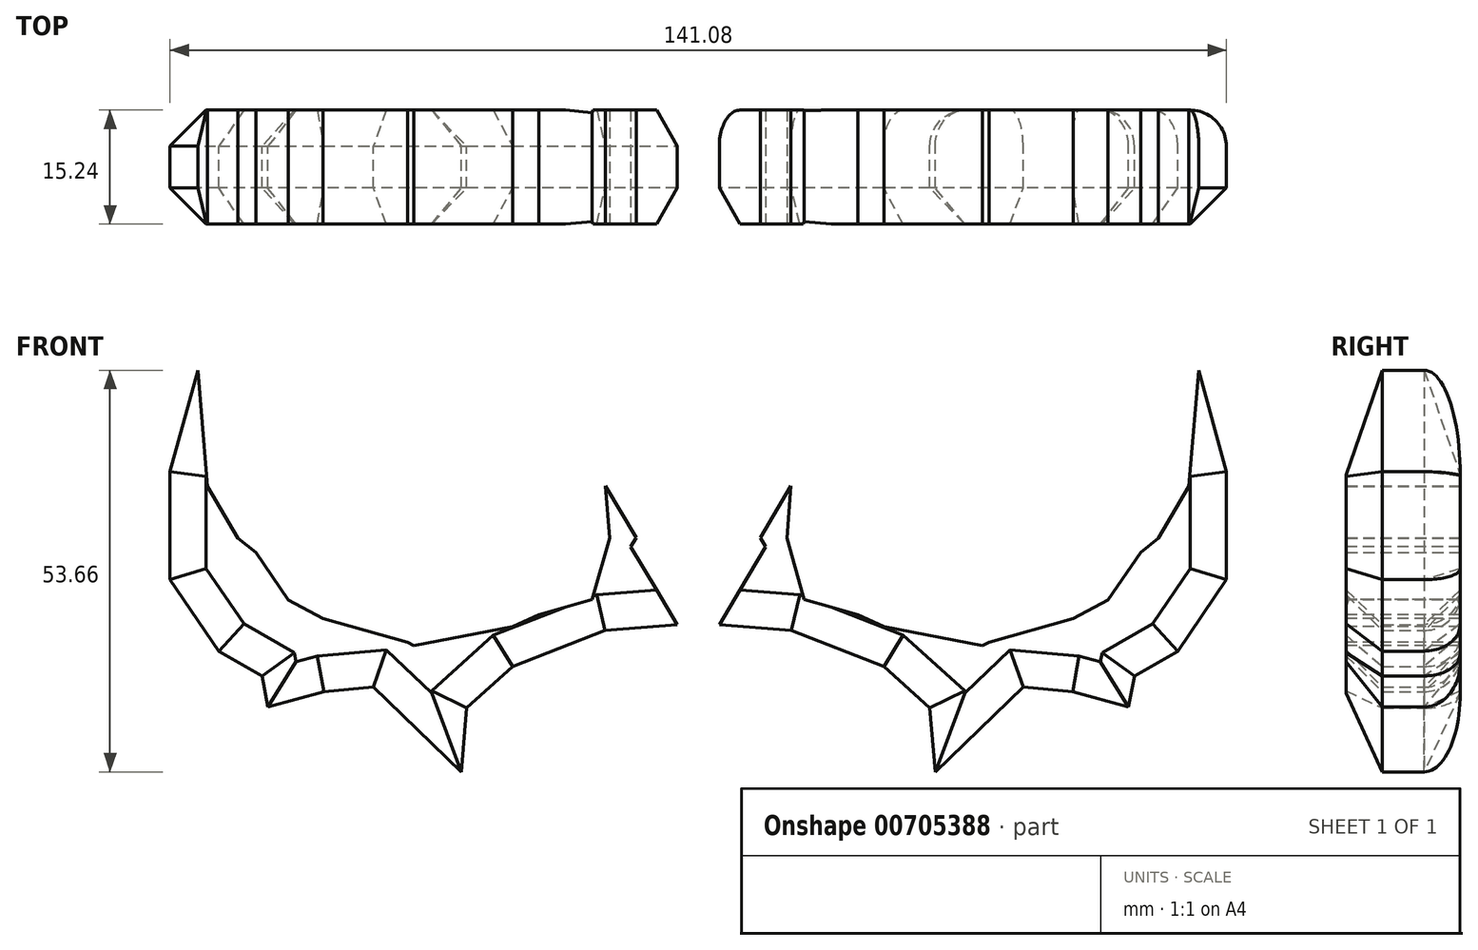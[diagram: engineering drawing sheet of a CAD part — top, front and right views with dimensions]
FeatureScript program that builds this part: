
annotation { "Feature Type Name" : "Feature", "Feature Type Description" : "" }
export const myFeature = defineFeature(function(context is Context, id is Id, definition is map)
    precondition{}
    {
        {
            var Q0;
            Q0=qCreatedBy(makeId("Front.planeOp"),FACE);
            var sketch = newSketch(context, id + "F0", { "sketchPlane" : qUnion([Q0])});
            skLineSegment(sketch, "E0", {"start": v(0, 0) * mm, "end": v(0, -3.04) * mm});
            skLineSegment(sketch, "E1", {"start": v(0, -3.04) * mm, "end": v(0, 0) * mm});
            skLineSegment(sketch, "E2", {"start": v(0, 15.49) * mm, "end": v(-8.28, 1.23) * mm});
            skLineSegment(sketch, "E3", {"start": v(-8.28, 1.23) * mm, "end": v(-12.37, 8.16) * mm});
            skLineSegment(sketch, "E4", {"start": v(-12.37, 8.16) * mm, "end": v(-11.9, 16.15) * mm});
            skFitSpline(sketch, "E5", {"points": [v(-11.9, 16.15) * mm, v(-15.37, 17.85) * mm, v(-17.68, 20.08) * mm, v(-20.4, 22.8) * mm, v(-21.58, 24.61) * mm, v(-23.4, 26.98) * mm], "startDerivative": vector(-17.13, 6.88) * mm, "endDerivative": vector(-10.36, 12.7) * mm});
            skLineSegment(sketch, "E6", {"start": v(-23.4, 26.98) * mm, "end": v(-23.4, 30.61) * mm});
            skLineSegment(sketch, "E7", {"start": v(-23.4, 30.61) * mm, "end": v(-28.49, 20.22) * mm});
            skFitSpline(sketch, "E8", {"points": [v(-28.49, 20.22) * mm, v(-23.37, 15.92) * mm, v(-19.88, 12.37) * mm, v(-18.57, 0.8) * mm], "startDerivative": vector(16.73, -14.68) * mm, "endDerivative": vector(0.35, -32.63) * mm});
            skLineSegment(sketch, "E9", {"start": v(-18.57, 0.8) * mm, "end": v(-25.11, 4.23) * mm});
            skFitSpline(sketch, "E10", {"points": [v(-25.11, 4.23) * mm, v(-32.14, 3.58) * mm, v(-37.97, 4.1) * mm, v(-37.97, 4.11) * mm, v(-37.98, 4.1) * mm], "startDerivative": vector(-12.52, -2.08) * mm, "endDerivative": vector(-0.69, -0.74) * mm});
            skLineSegment(sketch, "E11", {"start": v(-37.97, 4.11) * mm, "end": v(-43.4, 7.41) * mm});
            skLineSegment(sketch, "E12", {"start": v(-43.4, 7.41) * mm, "end": v(-46.92, 12.83) * mm});
            skLineSegment(sketch, "E13", {"start": v(-46.92, 12.83) * mm, "end": v(-48.7, 6.64) * mm});
            skLineSegment(sketch, "E14", {"start": v(-48.7, 6.64) * mm, "end": v(-46.89, 0.36) * mm});
            skLineSegment(sketch, "E15", {"start": v(-46.89, 0.36) * mm, "end": v(-50.1, 2.34) * mm});
            skLineSegment(sketch, "E16", {"start": v(-50.1, 2.34) * mm, "end": v(-54.25, 9.51) * mm});
            skLineSegment(sketch, "E17", {"start": v(-54.25, 9.51) * mm, "end": v(-56.92, 21.51) * mm});
            skLineSegment(sketch, "E18", {"start": v(-56.92, 21.51) * mm, "end": v(-60.41, 10.04) * mm});
            skLineSegment(sketch, "E19", {"start": v(-60.41, 10.04) * mm, "end": v(-59.08, -0.72) * mm});
            skLineSegment(sketch, "E20", {"start": v(-59.08, -0.72) * mm, "end": v(-61.47, 1.15) * mm});
            skLineSegment(sketch, "E21", {"start": v(-61.47, 1.15) * mm, "end": v(-65.53, 8.08) * mm});
            skLineSegment(sketch, "E22", {"start": v(-65.53, 8.08) * mm, "end": v(-66.84, 23.61) * mm});
            skLineSegment(sketch, "E23", {"start": v(-66.84, 23.61) * mm, "end": v(-70.54, 10.04) * mm});
            skLineSegment(sketch, "E24", {"start": v(-70.54, 10.04) * mm, "end": v(-70.54, -4.38) * mm});
            skLineSegment(sketch, "E25", {"start": v(-70.54, -4.38) * mm, "end": v(-64.04, -13.92) * mm});
            skLineSegment(sketch, "E26", {"start": v(-64.04, -13.92) * mm, "end": v(-58.26, -17.24) * mm});
            skLineSegment(sketch, "E27", {"start": v(-58.26, -17.24) * mm, "end": v(-57.47, -21.38) * mm});
            skLineSegment(sketch, "E28", {"start": v(-57.47, -21.38) * mm, "end": v(-50, -19.34) * mm});
            skLineSegment(sketch, "E29", {"start": v(-50, -19.34) * mm, "end": v(-43.4, -18.73) * mm});
            skLineSegment(sketch, "E30", {"start": v(-43.4, -18.73) * mm, "end": v(-31.64, -30.05) * mm});
            skLineSegment(sketch, "E31", {"start": v(-31.64, -30.05) * mm, "end": v(-30.93, -21.53) * mm});
            skLineSegment(sketch, "E32", {"start": v(-30.93, -21.53) * mm, "end": v(-24.8, -15.98) * mm});
            skLineSegment(sketch, "E33", {"start": v(-24.8, -15.98) * mm, "end": v(-12.45, -11.17) * mm});
            skLineSegment(sketch, "E34", {"start": v(-12.45, -11.17) * mm, "end": v(-2.8, -10.37) * mm});
            skLineSegment(sketch, "E35", {"start": v(-2.8, -10.37) * mm, "end": v(0, -15.23) * mm});
            skLineSegment(sketch, "E36", {"start": v(0, -15.23) * mm, "end": v(-2.8, -10.37) * mm});
            skLineSegment(sketch, "E37.MirrorCS", {"start": v(0, 15.49) * mm, "end": v(8.28, 1.23) * mm});
            skLineSegment(sketch, "E38.MirrorCS", {"start": v(0, -15.23) * mm, "end": v(2.8, -10.37) * mm});
            skLineSegment(sketch, "E39.MirrorCS", {"start": v(12.45, -11.17) * mm, "end": v(2.8, -10.37) * mm});
            skLineSegment(sketch, "E40.MirrorCS", {"start": v(8.28, 1.23) * mm, "end": v(12.37, 8.16) * mm});
            skLineSegment(sketch, "E41.MirrorCS", {"start": v(12.37, 8.16) * mm, "end": v(11.9, 16.15) * mm});
            skFitSpline(sketch, "E42.MirrorCS", {"points": [v(11.9, 16.15) * mm, v(15.37, 17.85) * mm, v(17.68, 20.08) * mm, v(20.4, 22.8) * mm, v(21.58, 24.61) * mm, v(23.4, 26.98) * mm], "startDerivative": vector(17.13, 6.88) * mm, "endDerivative": vector(10.36, 12.7) * mm});
            skLineSegment(sketch, "E43.MirrorCS", {"start": v(23.4, 30.61) * mm, "end": v(28.49, 20.22) * mm});
            skLineSegment(sketch, "E44.MirrorCS", {"start": v(23.4, 26.98) * mm, "end": v(23.4, 30.61) * mm});
            skFitSpline(sketch, "E45.MirrorCS", {"points": [v(28.49, 20.22) * mm, v(23.37, 15.92) * mm, v(19.88, 12.37) * mm, v(18.57, 0.8) * mm], "startDerivative": vector(-16.73, -14.68) * mm, "endDerivative": vector(-0.35, -32.63) * mm});
            skLineSegment(sketch, "E46.MirrorCS", {"start": v(18.57, 0.8) * mm, "end": v(25.11, 4.23) * mm});
            skFitSpline(sketch, "E47.MirrorCS", {"points": [v(25.11, 4.23) * mm, v(32.14, 3.58) * mm, v(37.97, 4.1) * mm, v(37.97, 4.11) * mm, v(37.98, 4.1) * mm], "startDerivative": vector(12.52, -2.08) * mm, "endDerivative": vector(0.69, -0.74) * mm});
            skLineSegment(sketch, "E48.MirrorCS", {"start": v(37.97, 4.11) * mm, "end": v(43.4, 7.41) * mm});
            skLineSegment(sketch, "E49.MirrorCS", {"start": v(43.4, 7.41) * mm, "end": v(46.92, 12.83) * mm});
            skLineSegment(sketch, "E50.MirrorCS", {"start": v(46.92, 12.83) * mm, "end": v(48.7, 6.64) * mm});
            skLineSegment(sketch, "E51.MirrorCS", {"start": v(48.7, 6.64) * mm, "end": v(46.89, 0.36) * mm});
            skLineSegment(sketch, "E52.MirrorCS", {"start": v(46.89, 0.36) * mm, "end": v(50.1, 2.34) * mm});
            skLineSegment(sketch, "E53.MirrorCS", {"start": v(50.1, 2.34) * mm, "end": v(54.25, 9.51) * mm});
            skLineSegment(sketch, "E54.MirrorCS", {"start": v(54.25, 9.51) * mm, "end": v(56.92, 21.51) * mm});
            skLineSegment(sketch, "E55.MirrorCS", {"start": v(56.92, 21.51) * mm, "end": v(60.41, 10.04) * mm});
            skLineSegment(sketch, "E56.MirrorCS", {"start": v(60.41, 10.04) * mm, "end": v(59.08, -0.72) * mm});
            skLineSegment(sketch, "E57.MirrorCS", {"start": v(59.08, -0.72) * mm, "end": v(61.47, 1.15) * mm});
            skLineSegment(sketch, "E58.MirrorCS", {"start": v(61.47, 1.15) * mm, "end": v(65.53, 8.08) * mm});
            skLineSegment(sketch, "E59.MirrorCS", {"start": v(65.53, 8.08) * mm, "end": v(66.84, 23.61) * mm});
            skLineSegment(sketch, "E60.MirrorCS", {"start": v(66.84, 23.61) * mm, "end": v(70.54, 10.04) * mm});
            skLineSegment(sketch, "E61.MirrorCS", {"start": v(70.54, 10.04) * mm, "end": v(70.54, -4.38) * mm});
            skLineSegment(sketch, "E62.MirrorCS", {"start": v(70.54, -4.38) * mm, "end": v(64.04, -13.92) * mm});
            skLineSegment(sketch, "E63.MirrorCS", {"start": v(64.04, -13.92) * mm, "end": v(58.26, -17.24) * mm});
            skLineSegment(sketch, "E64.MirrorCS", {"start": v(58.26, -17.24) * mm, "end": v(57.47, -21.38) * mm});
            skLineSegment(sketch, "E65.MirrorCS", {"start": v(57.47, -21.38) * mm, "end": v(50, -19.34) * mm});
            skLineSegment(sketch, "E66.MirrorCS", {"start": v(50, -19.34) * mm, "end": v(43.4, -18.73) * mm});
            skLineSegment(sketch, "E67.MirrorCS", {"start": v(43.4, -18.73) * mm, "end": v(31.64, -30.05) * mm});
            skLineSegment(sketch, "E68.MirrorCS", {"start": v(31.64, -30.05) * mm, "end": v(30.93, -21.53) * mm});
            skLineSegment(sketch, "E69.MirrorCS", {"start": v(30.93, -21.53) * mm, "end": v(24.8, -15.98) * mm});
            skLineSegment(sketch, "E70.MirrorCS", {"start": v(24.8, -15.98) * mm, "end": v(12.45, -11.17) * mm});
            skSolve(sketch);
        }
        {
            var Q0;
            Q0=makeQuery(id+"F0.imprint","IMPRINT",FACE,{"disambiguationData":[TD([[makeQuery(id+"F0.imprint","IMPRINT",EDGE,{"derivedFrom":sQuery(id+"F0.wireOp",EDGE,"E2")}),1.0]])]});
            extrude(context, id + "F1", {"entities" : qUnion([Q0]), "depth" : 7.62 * mm, "offsetDistance" : 25.4 * mm});
        }
        {
            var Q0;
            Q0=makeQuery(id+"F1.opExtrude","CAP_FACE",FACE,{"disambiguationData":[OSD([sQuery(id+"F0.wireOp",EDGE,"E2"),sQuery(id+"F0.wireOp",EDGE,"E3"),sQuery(id+"F0.wireOp",EDGE,"E4"),sQuery(id+"F0.wireOp",EDGE,"E5"),sQuery(id+"F0.wireOp",EDGE,"E6"),sQuery(id+"F0.wireOp",EDGE,"E7"),sQuery(id+"F0.wireOp",EDGE,"E8"),sQuery(id+"F0.wireOp",EDGE,"E9"),sQuery(id+"F0.wireOp",EDGE,"E10"),sQuery(id+"F0.wireOp",EDGE,"E11"),sQuery(id+"F0.wireOp",EDGE,"E12"),sQuery(id+"F0.wireOp",EDGE,"E13"),sQuery(id+"F0.wireOp",EDGE,"E14"),sQuery(id+"F0.wireOp",EDGE,"E15"),sQuery(id+"F0.wireOp",EDGE,"E16"),sQuery(id+"F0.wireOp",EDGE,"E17"),sQuery(id+"F0.wireOp",EDGE,"E18"),sQuery(id+"F0.wireOp",EDGE,"E19"),sQuery(id+"F0.wireOp",EDGE,"E20"),sQuery(id+"F0.wireOp",EDGE,"E21"),sQuery(id+"F0.wireOp",EDGE,"E22"),sQuery(id+"F0.wireOp",EDGE,"E23"),sQuery(id+"F0.wireOp",EDGE,"E24"),sQuery(id+"F0.wireOp",EDGE,"E25"),sQuery(id+"F0.wireOp",EDGE,"E26"),sQuery(id+"F0.wireOp",EDGE,"E27"),sQuery(id+"F0.wireOp",EDGE,"E28"),sQuery(id+"F0.wireOp",EDGE,"E29"),sQuery(id+"F0.wireOp",EDGE,"E30"),sQuery(id+"F0.wireOp",EDGE,"E31"),sQuery(id+"F0.wireOp",EDGE,"E32"),sQuery(id+"F0.wireOp",EDGE,"E33"),sQuery(id+"F0.wireOp",EDGE,"E34"),sQuery(id+"F0.wireOp",EDGE,"E36"),sQuery(id+"F0.wireOp",EDGE,"E37.MirrorCS"),sQuery(id+"F0.wireOp",EDGE,"E38.MirrorCS"),sQuery(id+"F0.wireOp",EDGE,"E39.MirrorCS"),sQuery(id+"F0.wireOp",EDGE,"E40.MirrorCS"),sQuery(id+"F0.wireOp",EDGE,"E41.MirrorCS"),sQuery(id+"F0.wireOp",EDGE,"E42.MirrorCS"),sQuery(id+"F0.wireOp",EDGE,"E43.MirrorCS"),sQuery(id+"F0.wireOp",EDGE,"E44.MirrorCS"),sQuery(id+"F0.wireOp",EDGE,"E45.MirrorCS"),sQuery(id+"F0.wireOp",EDGE,"E46.MirrorCS"),sQuery(id+"F0.wireOp",EDGE,"E47.MirrorCS"),sQuery(id+"F0.wireOp",EDGE,"E48.MirrorCS"),sQuery(id+"F0.wireOp",EDGE,"E49.MirrorCS"),sQuery(id+"F0.wireOp",EDGE,"E50.MirrorCS"),sQuery(id+"F0.wireOp",EDGE,"E51.MirrorCS"),sQuery(id+"F0.wireOp",EDGE,"E52.MirrorCS"),sQuery(id+"F0.wireOp",EDGE,"E53.MirrorCS"),sQuery(id+"F0.wireOp",EDGE,"E54.MirrorCS"),sQuery(id+"F0.wireOp",EDGE,"E55.MirrorCS"),sQuery(id+"F0.wireOp",EDGE,"E56.MirrorCS"),sQuery(id+"F0.wireOp",EDGE,"E57.MirrorCS"),sQuery(id+"F0.wireOp",EDGE,"E58.MirrorCS"),sQuery(id+"F0.wireOp",EDGE,"E59.MirrorCS"),sQuery(id+"F0.wireOp",EDGE,"E60.MirrorCS"),sQuery(id+"F0.wireOp",EDGE,"E61.MirrorCS"),sQuery(id+"F0.wireOp",EDGE,"E62.MirrorCS"),sQuery(id+"F0.wireOp",EDGE,"E63.MirrorCS"),sQuery(id+"F0.wireOp",EDGE,"E64.MirrorCS"),sQuery(id+"F0.wireOp",EDGE,"E65.MirrorCS"),sQuery(id+"F0.wireOp",EDGE,"E66.MirrorCS"),sQuery(id+"F0.wireOp",EDGE,"E67.MirrorCS"),sQuery(id+"F0.wireOp",EDGE,"E68.MirrorCS"),sQuery(id+"F0.wireOp",EDGE,"E69.MirrorCS"),sQuery(id+"F0.wireOp",EDGE,"E70.MirrorCS")])],"isStart":true});
            extrude(context, id + "F2", {"entities" : qUnion([Q0]), "operationType" : NewBodyOperationType.ADD, "depth" : 7.62 * mm, "offsetDistance" : 25.4 * mm});
        }
        {
            var Q0;
            Q0=makeQuery(id+"F1.opExtrude","CAP_FACE",FACE,{"disambiguationData":[OSD([sQuery(id+"F0.wireOp",EDGE,"E2"),sQuery(id+"F0.wireOp",EDGE,"E3"),sQuery(id+"F0.wireOp",EDGE,"E4"),sQuery(id+"F0.wireOp",EDGE,"E5"),sQuery(id+"F0.wireOp",EDGE,"E6"),sQuery(id+"F0.wireOp",EDGE,"E7"),sQuery(id+"F0.wireOp",EDGE,"E8"),sQuery(id+"F0.wireOp",EDGE,"E9"),sQuery(id+"F0.wireOp",EDGE,"E10"),sQuery(id+"F0.wireOp",EDGE,"E11"),sQuery(id+"F0.wireOp",EDGE,"E12"),sQuery(id+"F0.wireOp",EDGE,"E13"),sQuery(id+"F0.wireOp",EDGE,"E14"),sQuery(id+"F0.wireOp",EDGE,"E15"),sQuery(id+"F0.wireOp",EDGE,"E16"),sQuery(id+"F0.wireOp",EDGE,"E17"),sQuery(id+"F0.wireOp",EDGE,"E18"),sQuery(id+"F0.wireOp",EDGE,"E19"),sQuery(id+"F0.wireOp",EDGE,"E20"),sQuery(id+"F0.wireOp",EDGE,"E21"),sQuery(id+"F0.wireOp",EDGE,"E22"),sQuery(id+"F0.wireOp",EDGE,"E23"),sQuery(id+"F0.wireOp",EDGE,"E24"),sQuery(id+"F0.wireOp",EDGE,"E25"),sQuery(id+"F0.wireOp",EDGE,"E26"),sQuery(id+"F0.wireOp",EDGE,"E27"),sQuery(id+"F0.wireOp",EDGE,"E28"),sQuery(id+"F0.wireOp",EDGE,"E29"),sQuery(id+"F0.wireOp",EDGE,"E30"),sQuery(id+"F0.wireOp",EDGE,"E31"),sQuery(id+"F0.wireOp",EDGE,"E32"),sQuery(id+"F0.wireOp",EDGE,"E33"),sQuery(id+"F0.wireOp",EDGE,"E34"),sQuery(id+"F0.wireOp",EDGE,"E36"),sQuery(id+"F0.wireOp",EDGE,"E37.MirrorCS"),sQuery(id+"F0.wireOp",EDGE,"E38.MirrorCS"),sQuery(id+"F0.wireOp",EDGE,"E39.MirrorCS"),sQuery(id+"F0.wireOp",EDGE,"E40.MirrorCS"),sQuery(id+"F0.wireOp",EDGE,"E41.MirrorCS"),sQuery(id+"F0.wireOp",EDGE,"E42.MirrorCS"),sQuery(id+"F0.wireOp",EDGE,"E43.MirrorCS"),sQuery(id+"F0.wireOp",EDGE,"E44.MirrorCS"),sQuery(id+"F0.wireOp",EDGE,"E45.MirrorCS"),sQuery(id+"F0.wireOp",EDGE,"E46.MirrorCS"),sQuery(id+"F0.wireOp",EDGE,"E47.MirrorCS"),sQuery(id+"F0.wireOp",EDGE,"E48.MirrorCS"),sQuery(id+"F0.wireOp",EDGE,"E49.MirrorCS"),sQuery(id+"F0.wireOp",EDGE,"E50.MirrorCS"),sQuery(id+"F0.wireOp",EDGE,"E51.MirrorCS"),sQuery(id+"F0.wireOp",EDGE,"E52.MirrorCS"),sQuery(id+"F0.wireOp",EDGE,"E53.MirrorCS"),sQuery(id+"F0.wireOp",EDGE,"E54.MirrorCS"),sQuery(id+"F0.wireOp",EDGE,"E55.MirrorCS"),sQuery(id+"F0.wireOp",EDGE,"E56.MirrorCS"),sQuery(id+"F0.wireOp",EDGE,"E57.MirrorCS"),sQuery(id+"F0.wireOp",EDGE,"E58.MirrorCS"),sQuery(id+"F0.wireOp",EDGE,"E59.MirrorCS"),sQuery(id+"F0.wireOp",EDGE,"E60.MirrorCS"),sQuery(id+"F0.wireOp",EDGE,"E61.MirrorCS"),sQuery(id+"F0.wireOp",EDGE,"E62.MirrorCS"),sQuery(id+"F0.wireOp",EDGE,"E63.MirrorCS"),sQuery(id+"F0.wireOp",EDGE,"E64.MirrorCS"),sQuery(id+"F0.wireOp",EDGE,"E65.MirrorCS"),sQuery(id+"F0.wireOp",EDGE,"E66.MirrorCS"),sQuery(id+"F0.wireOp",EDGE,"E67.MirrorCS"),sQuery(id+"F0.wireOp",EDGE,"E68.MirrorCS"),sQuery(id+"F0.wireOp",EDGE,"E69.MirrorCS"),sQuery(id+"F0.wireOp",EDGE,"E70.MirrorCS")])],"isStart":false});
            var sketch = newSketch(context, id + "F3", { "sketchPlane" : qUnion([Q0])});
            skLineSegment(sketch, "E71", {"start": v(46.89, 0.36) * mm, "end": v(37.7, -5.04) * mm});
            skLineSegment(sketch, "E72", {"start": v(37.7, -5.04) * mm, "end": v(26.18, -4.3) * mm});
            skLineSegment(sketch, "E73", {"start": v(26.18, -4.3) * mm, "end": v(18.57, 0) * mm});
            skLineSegment(sketch, "E74", {"start": v(18.57, 0) * mm, "end": v(18.57, 0.8) * mm});
            skLineSegment(sketch, "E75", {"start": v(18.57, 0.8) * mm, "end": v(18.57, 0) * mm});
            skLineSegment(sketch, "E76", {"start": v(59.08, -0.72) * mm, "end": v(54.73, -7.1) * mm});
            skLineSegment(sketch, "E77", {"start": v(54.73, -7.1) * mm, "end": v(50.1, -9.58) * mm});
            skLineSegment(sketch, "E78", {"start": v(50.1, -9.58) * mm, "end": v(38.82, -12.7) * mm});
            skLineSegment(sketch, "E79", {"start": v(38.82, -12.7) * mm, "end": v(37.97, -13.2) * mm});
            skLineSegment(sketch, "E80", {"start": v(37.97, -13.2) * mm, "end": v(24.78, -10.64) * mm});
            skLineSegment(sketch, "E81", {"start": v(24.78, -10.64) * mm, "end": v(21.3, -9.07) * mm});
            skLineSegment(sketch, "E82", {"start": v(21.3, -9.07) * mm, "end": v(14.16, -7.03) * mm});
            skLineSegment(sketch, "E83", {"start": v(14.16, -7.03) * mm, "end": v(11.83, 1.15) * mm});
            skLineSegment(sketch, "E84", {"start": v(11.83, 1.15) * mm, "end": v(12.37, 8.16) * mm});
            skLineSegment(sketch, "E85", {"start": v(8.28, 1.23) * mm, "end": v(9, 0) * mm});
            skLineSegment(sketch, "E86", {"start": v(9, 0) * mm, "end": v(2.8, -10.37) * mm});
            skLineSegment(sketch, "E87", {"start": v(2.8, -10.37) * mm, "end": v(9, 0) * mm});
            skLineSegment(sketch, "E88", {"start": v(0, 0) * mm, "end": v(0, -1.55) * mm});
            skLineSegment(sketch, "E89", {"start": v(0, -1.55) * mm, "end": v(0, 0) * mm});
            skLineSegment(sketch, "E90.MirrorCS", {"start": v(-2.8, -10.37) * mm, "end": v(-9, 0) * mm});
            skLineSegment(sketch, "E91.MirrorCS", {"start": v(-8.28, 1.23) * mm, "end": v(-9, 0) * mm});
            skLineSegment(sketch, "E92.MirrorCS", {"start": v(-11.83, 1.15) * mm, "end": v(-12.37, 8.16) * mm});
            skLineSegment(sketch, "E93.MirrorCS", {"start": v(-14.16, -7.03) * mm, "end": v(-11.83, 1.15) * mm});
            skLineSegment(sketch, "E94.MirrorCS", {"start": v(-21.3, -9.07) * mm, "end": v(-14.16, -7.03) * mm});
            skLineSegment(sketch, "E95.MirrorCS", {"start": v(-24.78, -10.64) * mm, "end": v(-21.3, -9.07) * mm});
            skLineSegment(sketch, "E96.MirrorCS", {"start": v(-37.97, -13.2) * mm, "end": v(-24.78, -10.64) * mm});
            skLineSegment(sketch, "E97.MirrorCS", {"start": v(-50.1, -9.58) * mm, "end": v(-38.82, -12.7) * mm});
            skLineSegment(sketch, "E98.MirrorCS", {"start": v(-38.82, -12.7) * mm, "end": v(-37.97, -13.2) * mm});
            skLineSegment(sketch, "E99.MirrorCS", {"start": v(-54.73, -7.1) * mm, "end": v(-50.1, -9.58) * mm});
            skLineSegment(sketch, "E100.MirrorCS", {"start": v(-59.08, -0.72) * mm, "end": v(-54.73, -7.1) * mm});
            skLineSegment(sketch, "E101.MirrorCS", {"start": v(-46.89, 0.36) * mm, "end": v(-37.7, -5.04) * mm});
            skLineSegment(sketch, "E102.MirrorCS", {"start": v(-37.7, -5.04) * mm, "end": v(-26.18, -4.3) * mm});
            skLineSegment(sketch, "E103.MirrorCS", {"start": v(-26.18, -4.3) * mm, "end": v(-18.57, 0) * mm});
            skLineSegment(sketch, "E104.MirrorCS", {"start": v(-18.57, 0.8) * mm, "end": v(-18.57, 0) * mm});
            skSolve(sketch);
        }
        {
            var Q0;
            Q0=makeQuery(id+"F3.imprint","IMPRINT",FACE,{"disambiguationData":[TD([[makeQuery(id+"F3.imprint","IMPRINT",EDGE,{"derivedFrom":sQuery(id+"F3.wireOp",EDGE,"E71")}),1.0]])]});
            var Q1;
            Q1=makeQuery(id+"F3.imprint","IMPRINT",FACE,{"disambiguationData":[TD([[makeQuery(id+"F3.imprint","IMPRINT",EDGE,{"derivedFrom":sQuery(id+"F3.wireOp",EDGE,"E71")}),-1.0]])]});
            var Q2;
            Q2=makeQuery(id+"F3.imprint","IMPRINT",FACE,{"disambiguationData":[TD([[makeQuery(id+"F3.imprint","IMPRINT",EDGE,{"derivedFrom":sQuery(id+"F3.wireOp",EDGE,"E85")}),-1.0]])]});
            var Q3;
            Q3=makeQuery(id+"F3.imprint","IMPRINT",FACE,{"disambiguationData":[TD([[makeQuery(id+"F3.imprint","IMPRINT",EDGE,{"derivedFrom":sQuery(id+"F3.wireOp",EDGE,"E92.MirrorCS")}),1.0]])]});
            var Q4;
            Q4=makeQuery(id+"F3.imprint","IMPRINT",FACE,{"disambiguationData":[TD([[makeQuery(id+"F3.imprint","IMPRINT",EDGE,{"derivedFrom":sQuery(id+"F3.wireOp",EDGE,"E101.MirrorCS")}),1.0]])]});
            extrude(context, id + "F4", {"entities" : qUnion([Q0, Q1, Q2, Q3, Q4]), "operationType" : NewBodyOperationType.REMOVE, "oppositeDirection" : true, "depth" : 25.4 * mm, "offsetDistance" : 25.4 * mm});
        }
        {
            var Q0;
            Q0=makeQuery(id+"F1.opExtrude","CAP_EDGE",EDGE,{"disambiguationData":[OSD([sQuery(id+"F0.wireOp",EDGE,"E39.MirrorCS")])],"isStart":false});
            var Q1;
            Q1=makeQuery(id+"F1.opExtrude","CAP_EDGE",EDGE,{"disambiguationData":[OSD([sQuery(id+"F0.wireOp",EDGE,"E70.MirrorCS")])],"isStart":false});
            var Q2;
            Q2=makeQuery(id+"F1.opExtrude","CAP_EDGE",EDGE,{"disambiguationData":[OSD([sQuery(id+"F0.wireOp",EDGE,"E69.MirrorCS")])],"isStart":false});
            var Q3;
            Q3=makeQuery(id+"F1.opExtrude","CAP_EDGE",EDGE,{"disambiguationData":[OSD([sQuery(id+"F0.wireOp",EDGE,"E68.MirrorCS")])],"isStart":false});
            var Q4;
            Q4=makeQuery(id+"F1.opExtrude","CAP_EDGE",EDGE,{"disambiguationData":[OSD([sQuery(id+"F0.wireOp",EDGE,"E67.MirrorCS")])],"isStart":false});
            var Q5;
            Q5=makeQuery(id+"F1.opExtrude","CAP_EDGE",EDGE,{"disambiguationData":[OSD([sQuery(id+"F0.wireOp",EDGE,"E66.MirrorCS")])],"isStart":false});
            var Q6;
            Q6=makeQuery(id+"F1.opExtrude","CAP_EDGE",EDGE,{"disambiguationData":[OSD([sQuery(id+"F0.wireOp",EDGE,"E65.MirrorCS")])],"isStart":false});
            var Q7;
            Q7=makeQuery(id+"F1.opExtrude","CAP_EDGE",EDGE,{"disambiguationData":[OSD([sQuery(id+"F0.wireOp",EDGE,"E64.MirrorCS")])],"isStart":false});
            var Q8;
            Q8=makeQuery(id+"F1.opExtrude","CAP_EDGE",EDGE,{"disambiguationData":[OSD([sQuery(id+"F0.wireOp",EDGE,"E63.MirrorCS")])],"isStart":false});
            var Q9;
            Q9=makeQuery(id+"F1.opExtrude","CAP_EDGE",EDGE,{"disambiguationData":[OSD([sQuery(id+"F0.wireOp",EDGE,"E62.MirrorCS")])],"isStart":false});
            var Q10;
            Q10=makeQuery(id+"F1.opExtrude","CAP_EDGE",EDGE,{"disambiguationData":[OSD([sQuery(id+"F0.wireOp",EDGE,"E61.MirrorCS")])],"isStart":false});
            var Q11;
            Q11=makeQuery(id+"F1.opExtrude","CAP_EDGE",EDGE,{"disambiguationData":[OSD([sQuery(id+"F0.wireOp",EDGE,"E60.MirrorCS")])],"isStart":false});
            chamfer(context, id + "F5", {"entities" : qUnion([Q0, Q1, Q2, Q3, Q4, Q5, Q6, Q7, Q8, Q9, Q10, Q11]), "width" : 4.83 * mm, "tangentPropagation" : true});
        }
        {
            var Q0;
            Q0=makeQuery(id+"F1.opExtrude","CAP_EDGE",EDGE,{"disambiguationData":[OSD([sQuery(id+"F0.wireOp",EDGE,"E34")])],"isStart":false});
            var Q1;
            Q1=makeQuery(id+"F1.opExtrude","CAP_EDGE",EDGE,{"disambiguationData":[OSD([sQuery(id+"F0.wireOp",EDGE,"E33")])],"isStart":false});
            var Q2;
            Q2=makeQuery(id+"F1.opExtrude","CAP_EDGE",EDGE,{"disambiguationData":[OSD([sQuery(id+"F0.wireOp",EDGE,"E32")])],"isStart":false});
            var Q3;
            Q3=makeQuery(id+"F1.opExtrude","CAP_EDGE",EDGE,{"disambiguationData":[OSD([sQuery(id+"F0.wireOp",EDGE,"E31")])],"isStart":false});
            var Q4;
            Q4=makeQuery(id+"F1.opExtrude","CAP_EDGE",EDGE,{"disambiguationData":[OSD([sQuery(id+"F0.wireOp",EDGE,"E30")])],"isStart":false});
            var Q5;
            Q5=makeQuery(id+"F1.opExtrude","CAP_EDGE",EDGE,{"disambiguationData":[OSD([sQuery(id+"F0.wireOp",EDGE,"E29")])],"isStart":false});
            var Q6;
            Q6=makeQuery(id+"F1.opExtrude","CAP_EDGE",EDGE,{"disambiguationData":[OSD([sQuery(id+"F0.wireOp",EDGE,"E28")])],"isStart":false});
            var Q7;
            Q7=makeQuery(id+"F1.opExtrude","CAP_EDGE",EDGE,{"disambiguationData":[OSD([sQuery(id+"F0.wireOp",EDGE,"E27")])],"isStart":false});
            var Q8;
            Q8=makeQuery(id+"F1.opExtrude","CAP_EDGE",EDGE,{"disambiguationData":[OSD([sQuery(id+"F0.wireOp",EDGE,"E26")])],"isStart":false});
            var Q9;
            Q9=makeQuery(id+"F1.opExtrude","CAP_EDGE",EDGE,{"disambiguationData":[OSD([sQuery(id+"F0.wireOp",EDGE,"E25")])],"isStart":false});
            var Q10;
            Q10=makeQuery(id+"F1.opExtrude","CAP_EDGE",EDGE,{"disambiguationData":[OSD([sQuery(id+"F0.wireOp",EDGE,"E24")])],"isStart":false});
            var Q11;
            Q11=makeQuery(id+"F1.opExtrude","CAP_EDGE",EDGE,{"disambiguationData":[OSD([sQuery(id+"F0.wireOp",EDGE,"E23")])],"isStart":false});
            chamfer(context, id + "F6", {"entities" : qUnion([Q0, Q1, Q2, Q3, Q4, Q5, Q6, Q7, Q8, Q9, Q10, Q11]), "width" : 4.83 * mm, "tangentPropagation" : true});
        }
        {
            var Q0;
            Q0=makeQuery(id+"F2.opExtrude","CAP_EDGE",EDGE,{"disambiguationData":[OSD([sQuery(id+"F0.wireOp",EDGE,"E23")])],"isStart":false});
            var Q1;
            Q1=makeQuery(id+"F2.opExtrude","CAP_EDGE",EDGE,{"disambiguationData":[OSD([sQuery(id+"F0.wireOp",EDGE,"E24")])],"isStart":false});
            var Q2;
            Q2=makeQuery(id+"F2.opExtrude","CAP_EDGE",EDGE,{"disambiguationData":[OSD([sQuery(id+"F0.wireOp",EDGE,"E25")])],"isStart":false});
            var Q3;
            Q3=makeQuery(id+"F2.opExtrude","CAP_EDGE",EDGE,{"disambiguationData":[OSD([sQuery(id+"F0.wireOp",EDGE,"E26")])],"isStart":false});
            var Q4;
            Q4=makeQuery(id+"F2.opExtrude","CAP_EDGE",EDGE,{"disambiguationData":[OSD([sQuery(id+"F0.wireOp",EDGE,"E27")])],"isStart":false});
            var Q5;
            Q5=makeQuery(id+"F2.opExtrude","CAP_EDGE",EDGE,{"disambiguationData":[OSD([sQuery(id+"F0.wireOp",EDGE,"E28")])],"isStart":false});
            var Q6;
            Q6=makeQuery(id+"F2.opExtrude","CAP_EDGE",EDGE,{"disambiguationData":[OSD([sQuery(id+"F0.wireOp",EDGE,"E29")])],"isStart":false});
            var Q7;
            Q7=makeQuery(id+"F2.opExtrude","CAP_EDGE",EDGE,{"disambiguationData":[OSD([sQuery(id+"F0.wireOp",EDGE,"E30")])],"isStart":false});
            var Q8;
            Q8=makeQuery(id+"F2.opExtrude","CAP_EDGE",EDGE,{"disambiguationData":[OSD([sQuery(id+"F0.wireOp",EDGE,"E31")])],"isStart":false});
            var Q9;
            Q9=makeQuery(id+"F2.opExtrude","CAP_EDGE",EDGE,{"disambiguationData":[OSD([sQuery(id+"F0.wireOp",EDGE,"E32")])],"isStart":false});
            var Q10;
            Q10=makeQuery(id+"F2.opExtrude","CAP_EDGE",EDGE,{"disambiguationData":[OSD([sQuery(id+"F0.wireOp",EDGE,"E33")])],"isStart":false});
            var Q11;
            Q11=makeQuery(id+"F2.opExtrude","CAP_EDGE",EDGE,{"disambiguationData":[OSD([sQuery(id+"F0.wireOp",EDGE,"E34")])],"isStart":false});
            chamfer(context, id + "F7", {"entities" : qUnion([Q0, Q1, Q2, Q3, Q4, Q5, Q6, Q7, Q8, Q9, Q10, Q11]), "width" : 4.83 * mm, "tangentPropagation" : true});
        }
        {
            var Q0;
            Q0=makeQuery(id+"F2.opExtrude","CAP_EDGE",EDGE,{"disambiguationData":[OSD([sQuery(id+"F0.wireOp",EDGE,"E39.MirrorCS")])],"isStart":false});
            var Q1;
            Q1=makeQuery(id+"F2.opExtrude","CAP_EDGE",EDGE,{"disambiguationData":[OSD([sQuery(id+"F0.wireOp",EDGE,"E70.MirrorCS")])],"isStart":false});
            var Q2;
            Q2=makeQuery(id+"F2.opExtrude","CAP_EDGE",EDGE,{"disambiguationData":[OSD([sQuery(id+"F0.wireOp",EDGE,"E69.MirrorCS")])],"isStart":false});
            var Q3;
            Q3=makeQuery(id+"F2.opExtrude","CAP_EDGE",EDGE,{"disambiguationData":[OSD([sQuery(id+"F0.wireOp",EDGE,"E68.MirrorCS")])],"isStart":false});
            var Q4;
            Q4=makeQuery(id+"F2.opExtrude","CAP_EDGE",EDGE,{"disambiguationData":[OSD([sQuery(id+"F0.wireOp",EDGE,"E67.MirrorCS")])],"isStart":false});
            var Q5;
            Q5=makeQuery(id+"F2.opExtrude","CAP_EDGE",EDGE,{"disambiguationData":[OSD([sQuery(id+"F0.wireOp",EDGE,"E66.MirrorCS")])],"isStart":false});
            var Q6;
            Q6=makeQuery(id+"F2.opExtrude","CAP_EDGE",EDGE,{"disambiguationData":[OSD([sQuery(id+"F0.wireOp",EDGE,"E65.MirrorCS")])],"isStart":false});
            var Q7;
            Q7=makeQuery(id+"F2.opExtrude","CAP_EDGE",EDGE,{"disambiguationData":[OSD([sQuery(id+"F0.wireOp",EDGE,"E64.MirrorCS")])],"isStart":false});
            var Q8;
            Q8=makeQuery(id+"F2.opExtrude","CAP_EDGE",EDGE,{"disambiguationData":[OSD([sQuery(id+"F0.wireOp",EDGE,"E63.MirrorCS")])],"isStart":false});
            var Q9;
            Q9=makeQuery(id+"F2.opExtrude","CAP_EDGE",EDGE,{"disambiguationData":[OSD([sQuery(id+"F0.wireOp",EDGE,"E62.MirrorCS")])],"isStart":false});
            var Q10;
            Q10=makeQuery(id+"F2.opExtrude","CAP_EDGE",EDGE,{"disambiguationData":[OSD([sQuery(id+"F0.wireOp",EDGE,"E61.MirrorCS")])],"isStart":false});
            var Q11;
            Q11=makeQuery(id+"F2.opExtrude","CAP_EDGE",EDGE,{"disambiguationData":[OSD([sQuery(id+"F0.wireOp",EDGE,"E60.MirrorCS")])],"isStart":false});
            fillet(context, id + "F8", {"entities" : qUnion([Q0, Q1, Q2, Q3, Q4, Q5, Q6, Q7, Q8, Q9, Q10, Q11]), "radius" : 4.83 * mm, "tangentPropagation" : true, "allowEdgeOverflow" : false});
        }
    });
